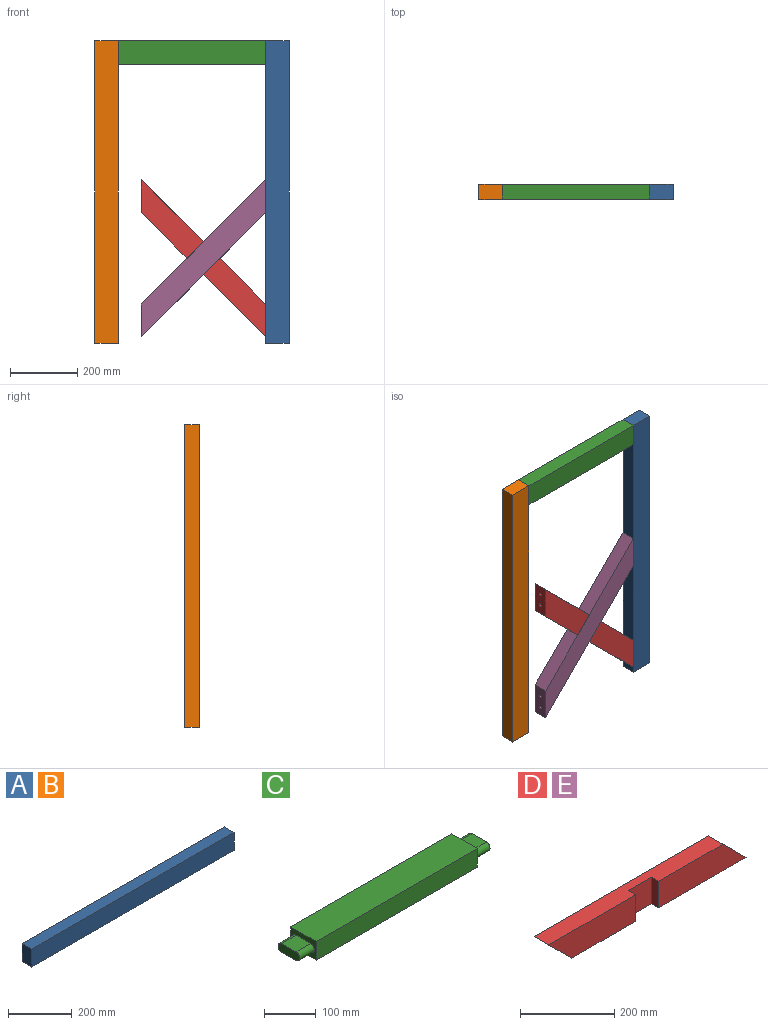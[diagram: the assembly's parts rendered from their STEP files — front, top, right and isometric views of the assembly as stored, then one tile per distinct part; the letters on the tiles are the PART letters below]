
ASSEMBLY  parts=5 mates=4
PART A: 11 faces, bbox 900x44x69 mm
  f0: plane 900x44mm, normal (0,0,-1), area 38505.8mm2, adj f2,f3,f4,f5,f6,f7,f8,f9
  f1: plane 900x44mm, normal (0,0,1), area 39600mm2, adj f2,f3,f4,f5
  f2: plane 900x69mm, normal (0,-1,0), area 62100mm2, adj f0,f1,f4,f5
  f3: plane 900x69mm, normal (0,1,0), area 62100mm2, adj f0,f1,f4,f5
  f4: plane 69x44mm, normal (1,0,0), area 3036mm2, adj f0,f1,f2,f3
  f5: plane 69x44mm, normal (-1,0,0), area 3036mm2, adj f0,f1,f2,f3
  f6: plane 40x39mm, normal (0,-1,0), area 1560mm2, adj f0,f7,f9,f10
  f7: cylinder r=10mm len=40mm, axis (0,0,-1), area 1256.6mm2, adj f0,f6,f8,f10
  f8: plane 40x39mm, normal (0,1,0), area 1560mm2, adj f0,f7,f9,f10
  f9: cylinder r=10mm len=40mm, axis (0,0,-1), area 1256.6mm2, adj f0,f6,f8,f10
  f10: plane 59x20mm, normal (0,0,-1), area 1094.2mm2, adj f6,f7,f8,f9
PART B: same geometry as A
PART C: 16 faces, bbox 520x69x44 mm
  f0: plane 69x44mm, normal (1,0,0), area 1941.8mm2, adj f2,f3,f4,f5,f11,f12,f13,f14
  f1: plane 69x44mm, normal (-1,0,0), area 1941.8mm2, adj f2,f3,f4,f5,f6,f7,f8,f9
  f2: plane 440x69mm, normal (0,0,1), area 30360mm2, adj f0,f1,f3,f5
  f3: plane 440x44mm, normal (0,-1,0), area 19360mm2, adj f0,f1,f2,f4
  f4: plane 440x69mm, normal (0,0,-1), area 30360mm2, adj f0,f1,f3,f5
  f5: plane 440x44mm, normal (0,1,0), area 19360mm2, adj f0,f1,f2,f4
  f6: plane 40x39mm, normal (0,0,1), area 1560mm2, adj f1,f7,f9,f10
  f7: cylinder r=10mm len=40mm, axis (1,0,0), area 1256.6mm2, adj f1,f6,f8,f10
  f8: plane 40x39mm, normal (0,0,-1), area 1560mm2, adj f1,f7,f9,f10
  f9: cylinder r=10mm len=40mm, axis (1,0,0), area 1256.6mm2, adj f1,f6,f8,f10
  f10: plane 59x20mm, normal (-1,0,0), area 1094.2mm2, adj f6,f7,f8,f9
  f11: plane 40x39mm, normal (0,0,-1), area 1560mm2, adj f0,f12,f14,f15
  f12: cylinder r=10mm len=40mm, axis (-1,0,0), area 1256.6mm2, adj f0,f11,f13,f15
  f13: plane 40x39mm, normal (0,0,1), area 1560mm2, adj f0,f12,f14,f15
  f14: cylinder r=10mm len=40mm, axis (-1,0,0), area 1256.6mm2, adj f0,f11,f13,f15
  f15: plane 59x20mm, normal (1,0,0), area 1094.2mm2, adj f11,f12,f13,f14
PART D: 18 faces, bbox 593x44x69 mm
  f0: plane 262x69mm, normal (0,-1,0), area 15697.5mm2, adj f2,f3,f10,f15
  f1: plane 261x69mm, normal (0,-1,0), area 15628.5mm2, adj f2,f3,f5,f16
  f2: plane 524x44mm, normal (0,0,1), area 21516mm2, adj f0,f1,f4,f5,f10,f15,f16,f17
  f3: plane 524x44mm, normal (0,0,-1), area 21516mm2, adj f0,f1,f4,f5,f10,f15,f16,f17
  f4: plane 593x69mm, normal (0,1,0), area 36156mm2, adj f2,f3,f5,f10
  f5: plane 69x69mm, normal (-0.71,0,-0.71), area 4193mm2, adj f1,f2,f3,f4,f7,f9
  f6: cone r=0mm half-angle=59deg, axis (-0.71,0,-0.71), area 58.6mm2, adj f7
  f7: cylinder r=4mm len=19.8mm, axis (-0.71,0,-0.71), area 502.7mm2, adj f5,f6
  f8: cone r=0mm half-angle=59deg, axis (-0.71,0,-0.71), area 58.6mm2, adj f9
  f9: cylinder r=4mm len=19.8mm, axis (-0.71,0,-0.71), area 502.7mm2, adj f5,f8
  f10: plane 69x69mm, normal (0.71,0,0.71), area 4193mm2, adj f0,f2,f3,f4,f12,f14
  f11: cone r=0mm half-angle=59deg, axis (0.71,0,0.71), area 58.6mm2, adj f12
  f12: cylinder r=4mm len=19.8mm, axis (0.71,0,0.71), area 502.7mm2, adj f10,f11
  f13: cone r=0mm half-angle=59deg, axis (0.71,0,0.71), area 58.6mm2, adj f14
  f14: cylinder r=4mm len=19.8mm, axis (0.71,0,0.71), area 502.7mm2, adj f10,f13
  f15: plane 69x22mm, normal (-1,0,0), area 1518mm2, adj f0,f2,f3,f17
  f16: plane 69x22mm, normal (1,0,0), area 1518mm2, adj f1,f2,f3,f17
  f17: plane 70x69mm, normal (0,-1,0), area 4830mm2, adj f2,f3,f15,f16
PART E: same geometry as D
PLACE A rot(axis=(-0.71,0,-0.71),180deg) t=(436.22,-40.7,-807.41)mm
PLACE B rot(axis=(0,-1,0),90deg) t=(-3.78,-43.74,-807.41)mm
PLACE C rot(axis=(1,0,0),90deg) t=(-3.78,-56.76,61.24)mm
PLACE D rot(axis=(0,1,0),45deg) t=(38.19,-44.55,-348.64)mm
PLACE E rot(axis=(-0.92,0,-0.38),180deg) t=(38.19,-39.87,-761.03)mm
MATE fastened B.f10 <-> C.f10  axis (1,0,0) through (-43.78,-42.22,58.09)mm
MATE fastened E.f17 <-> D.f17  axis (0,1,0) through (250.61,-42.21,-554.84)mm
MATE fastened A.f10 <-> C.f15  axis (-1,0,0) through (476.22,-42.22,58.09)mm
MATE fastened E.f10 <-> A.f0  axis (1,0,0) through (436.22,-42.22,-369.22)mm
